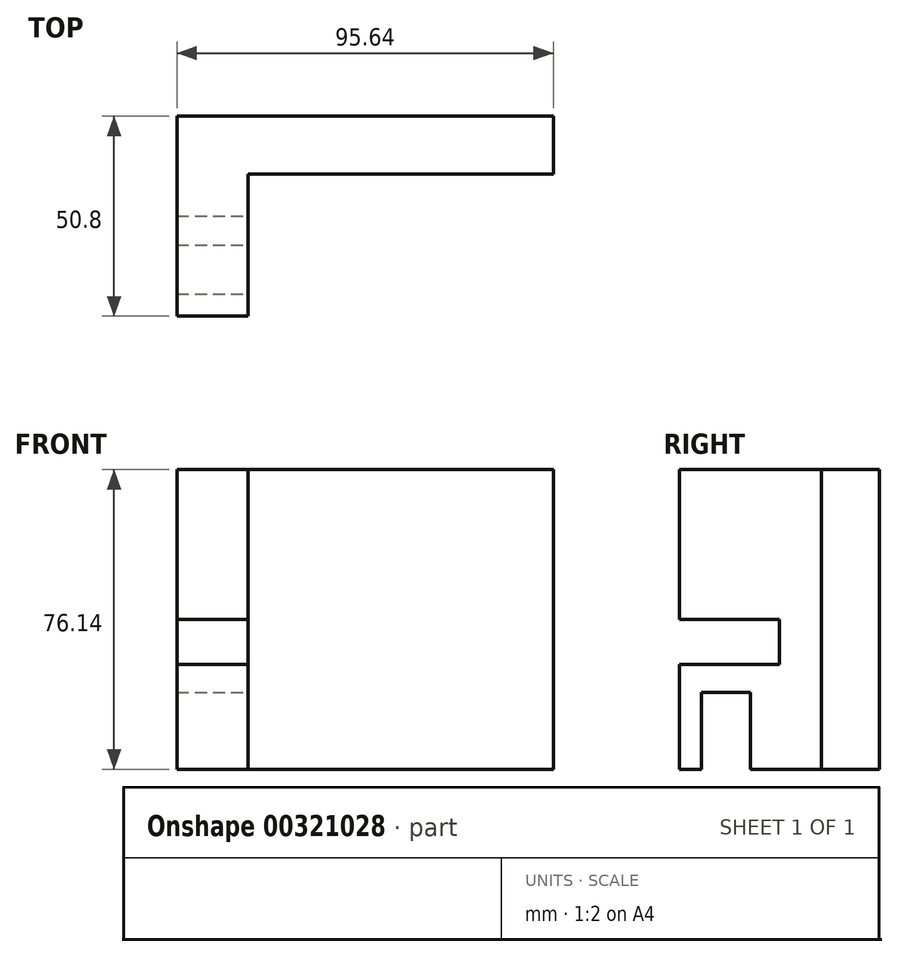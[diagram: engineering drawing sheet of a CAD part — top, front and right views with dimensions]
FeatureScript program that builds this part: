
annotation { "Feature Type Name" : "Feature", "Feature Type Description" : "" }
export const myFeature = defineFeature(function(context is Context, id is Id, definition is map)
    precondition{}
    {
        {
            var Q0;
            Q0=qCreatedBy(makeId("Front.planeOp"),FACE);
            var sketch = newSketch(context, id + "F0", { "sketchPlane" : qUnion([Q0])});
            skLineSegment(sketch, "E0.bottom", {"start": v(-44.26, 23.06) * mm, "end": v(51.38, 23.06) * mm});
            skLineSegment(sketch, "E0.top", {"start": v(-44.26, -53.08) * mm, "end": v(51.38, -53.08) * mm});
            skLineSegment(sketch, "E0.left", {"start": v(-44.26, 23.06) * mm, "end": v(-44.26, -53.08) * mm});
            skLineSegment(sketch, "E0.right", {"start": v(51.38, 23.06) * mm, "end": v(51.38, -53.08) * mm});
            skSolve(sketch);
        }
        {
            var Q0;
            Q0=makeQuery(id+"F0.imprint","IMPRINT",FACE,{"disambiguationData":[TD([[makeQuery(id+"F0.imprint","IMPRINT",EDGE,{"derivedFrom":sQuery(id+"F0.wireOp",EDGE,"E0.bottom")}),-1.0]])]});
            extrude(context, id + "F1", {"entities" : qUnion([Q0]), "depth" : 50.8 * mm});
        }
        {
            var Q0;
            Q0=makeQuery(id+"F1.opExtrude","SWEPT_FACE",FACE,{"disambiguationData":[OSD([sQuery(id+"F0.wireOp",EDGE,"E0.bottom")])]});
            var sketch = newSketch(context, id + "F2", { "sketchPlane" : qUnion([Q0])});
            skLineSegment(sketch, "E1.bottom", {"start": v(-26.24, -50.8) * mm, "end": v(51.38, -50.8) * mm});
            skLineSegment(sketch, "E1.top", {"start": v(-26.24, -14.66) * mm, "end": v(51.38, -14.66) * mm});
            skLineSegment(sketch, "E1.left", {"start": v(-26.24, -50.8) * mm, "end": v(-26.24, -14.66) * mm});
            skLineSegment(sketch, "E1.right", {"start": v(51.38, -50.8) * mm, "end": v(51.38, -14.66) * mm});
            skSolve(sketch);
        }
        {
            var Q0;
            Q0=makeQuery(id+"F2.imprint","IMPRINT",FACE,{"disambiguationData":[TD([[makeQuery(id+"F2.imprint","IMPRINT",EDGE,{"derivedFrom":sQuery(id+"F2.wireOp",EDGE,"E1.bottom")}),1.0]])]});
            extrude(context, id + "F3", {"entities" : qUnion([Q0]), "operationType" : NewBodyOperationType.REMOVE, "endBound" : BoundingType.THROUGH_ALL, "oppositeDirection" : true, "depth" : 25.4 * mm});
        }
        {
            var Q0;
            Q0=makeQuery(id+"F1.opExtrude","CAP_FACE",FACE,{"disambiguationData":[OSD([sQuery(id+"F0.wireOp",EDGE,"E0.bottom"),sQuery(id+"F0.wireOp",EDGE,"E0.top"),sQuery(id+"F0.wireOp",EDGE,"E0.left"),sQuery(id+"F0.wireOp",EDGE,"E0.right")])],"isStart":false});
            var sketch = newSketch(context, id + "F4", { "sketchPlane" : qUnion([Q0])});
            skLineSegment(sketch, "E2.bottom", {"start": v(-44.26, -15.01) * mm, "end": v(-26.24, -15.01) * mm});
            skLineSegment(sketch, "E2.top", {"start": v(-44.26, -26.37) * mm, "end": v(-26.24, -26.37) * mm});
            skLineSegment(sketch, "E2.left", {"start": v(-44.26, -15.01) * mm, "end": v(-44.26, -26.37) * mm});
            skLineSegment(sketch, "E2.right", {"start": v(-26.24, -15.01) * mm, "end": v(-26.24, -26.37) * mm});
            skSolve(sketch);
        }
        {
            var Q0;
            Q0=makeQuery(id+"F4.imprint","IMPRINT",FACE,{"disambiguationData":[TD([[makeQuery(id+"F4.imprint","IMPRINT",EDGE,{"derivedFrom":sQuery(id+"F4.wireOp",EDGE,"E2.bottom")}),-1.0]])]});
            extrude(context, id + "F5", {"entities" : qUnion([Q0]), "operationType" : NewBodyOperationType.REMOVE, "oppositeDirection" : true, "depth" : 25.4 * mm});
        }
        {
            var Q0;
            Q0=makeQuery(id+"F3.boolean.opBoolean","COPY",FACE,{"derivedFrom":makeQuery(id+"F3.opExtrude","SWEPT_FACE",FACE,{"disambiguationData":[OSD([sQuery(id+"F2.wireOp",EDGE,"E1.left")])]})});
            var sketch = newSketch(context, id + "F6", { "sketchPlane" : qUnion([Q0])});
            skLineSegment(sketch, "E3.bottom", {"start": v(-32.73, -53.08) * mm, "end": v(-45.15, -53.08) * mm});
            skLineSegment(sketch, "E3.top", {"start": v(-32.73, -33.5) * mm, "end": v(-45.15, -33.5) * mm});
            skLineSegment(sketch, "E3.left", {"start": v(-32.73, -53.08) * mm, "end": v(-32.73, -33.5) * mm});
            skLineSegment(sketch, "E3.right", {"start": v(-45.15, -53.08) * mm, "end": v(-45.15, -33.5) * mm});
            skSolve(sketch);
        }
        {
            var Q0;
            Q0=makeQuery(id+"F6.imprint","IMPRINT",FACE,{"disambiguationData":[TD([[makeQuery(id+"F6.imprint","IMPRINT",EDGE,{"derivedFrom":sQuery(id+"F6.wireOp",EDGE,"E3.bottom")}),1.0]])]});
            extrude(context, id + "F7", {"entities" : qUnion([Q0]), "operationType" : NewBodyOperationType.REMOVE, "oppositeDirection" : true, "depth" : 25.4 * mm});
        }
    });
